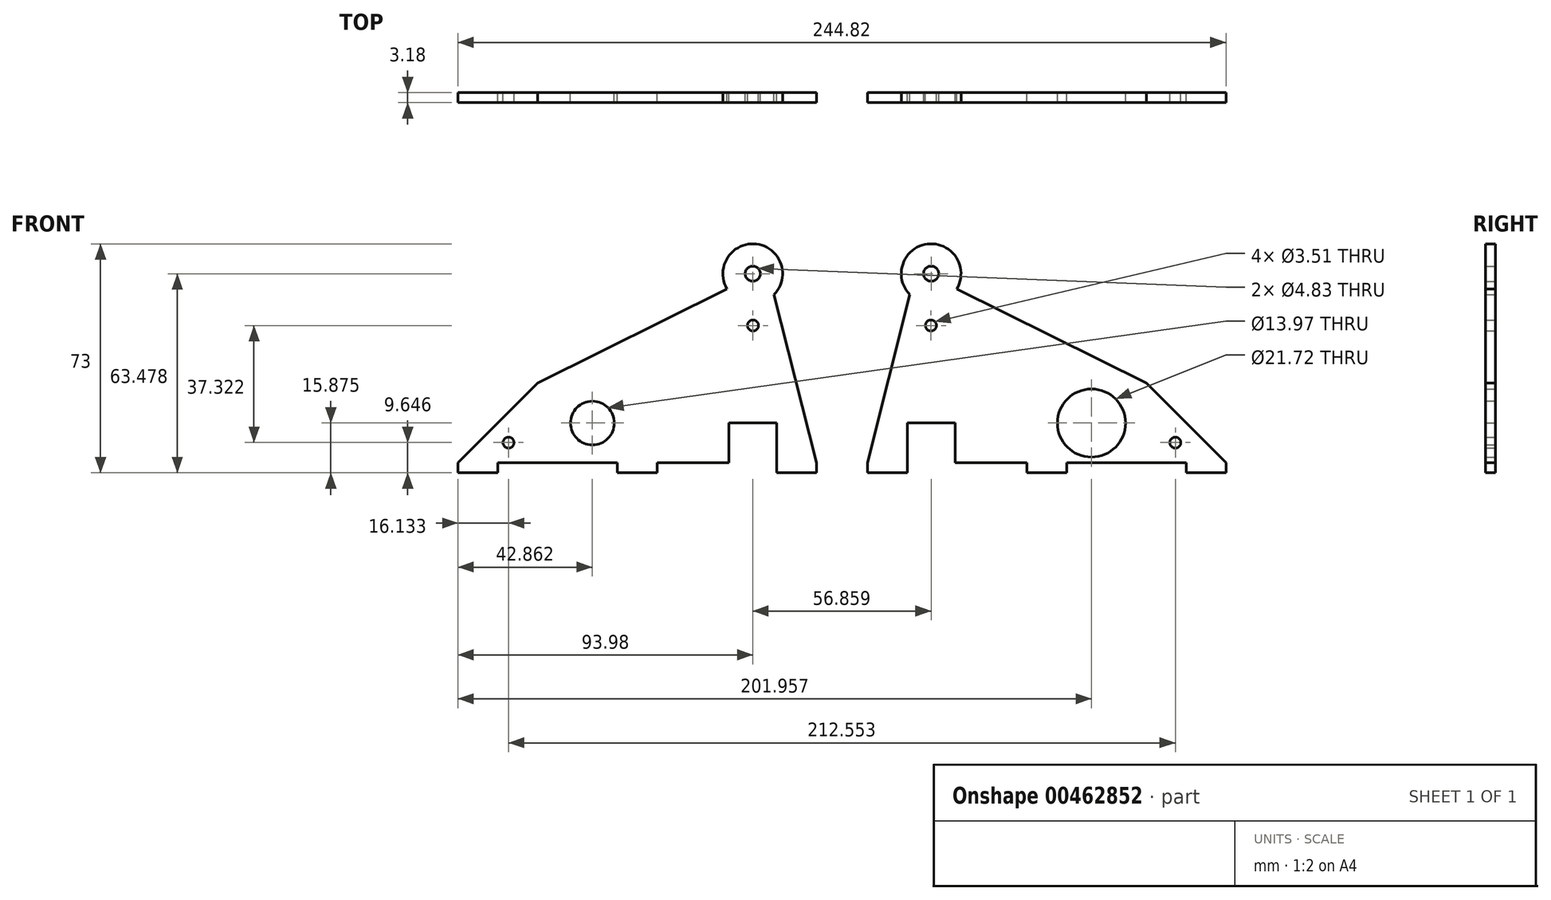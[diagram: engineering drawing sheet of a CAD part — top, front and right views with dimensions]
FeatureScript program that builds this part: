
annotation { "Feature Type Name" : "Feature", "Feature Type Description" : "" }
export const myFeature = defineFeature(function(context is Context, id is Id, definition is map)
    precondition{}
    {
        {
            var Q0;
            Q0=qCreatedBy(makeId("Front.planeOp"),FACE);
            var sketch = newSketch(context, id + "F0", { "sketchPlane" : qUnion([Q0])});
            skPoint(sketch, "E0.middle", {"position": v(0, 0) * mm});
            skLineSegment(sketch, "E1.bottom", {"start": v(-50.8, -34.93) * mm, "end": v(-12.7, -34.93) * mm});
            skLineSegment(sketch, "E1.left", {"start": v(-63.5, -34.92) * mm, "end": v(-63.5, -38.1) * mm});
            skLineSegment(sketch, "E2", {"start": v(-12.7, -34.93) * mm, "end": v(-12.7, -38.1) * mm});
            skLineSegment(sketch, "E3", {"start": v(0, -34.93) * mm, "end": v(0, -38.1) * mm});
            skLineSegment(sketch, "E4", {"start": v(50.8, -34.93) * mm, "end": v(50.8, -38.1) * mm});
            skLineSegment(sketch, "E5", {"start": v(38.1, -34.93) * mm, "end": v(38.1, -38.1) * mm});
            skLineSegment(sketch, "E6.trimOffspring", {"start": v(-12.7, -38.1) * mm, "end": v(0, -38.1) * mm});
            skLineSegment(sketch, "E7.trimOffspring", {"start": v(38.1, -38.1) * mm, "end": v(50.8, -38.1) * mm});
            skLineSegment(sketch, "E8", {"start": v(-38.1, -34.93) * mm, "end": v(-38.1, -9.53) * mm});
            skLineSegment(sketch, "E9", {"start": v(-38.1, -9.53) * mm, "end": v(-3.17, -9.53) * mm});
            skLineSegment(sketch, "E10", {"start": v(-3.17, -9.53) * mm, "end": v(-3.17, -34.92) * mm});
            skLineSegment(sketch, "E11", {"start": v(-38.1, -22.23) * mm, "end": v(-20.64, -22.23) * mm});
            skCircle(sketch, "E12", {"center": v(-20.64, -22.23) * mm, "radius": 6.99 * mm});
            skLineSegment(sketch, "E13", {"start": v(38.1, -34.93) * mm, "end": v(38.1, -22.23) * mm});
            skLineSegment(sketch, "E14", {"start": v(38.1, -22.22) * mm, "end": v(22.86, -22.23) * mm});
            skLineSegment(sketch, "E15", {"start": v(22.86, -22.23) * mm, "end": v(22.86, -34.93) * mm});
            skCircle(sketch, "E16", {"center": v(30.48, 25.38) * mm, "radius": 2.41 * mm});
            skCircle(sketch, "E17", {"center": v(30.48, 25.38) * mm, "radius": 9.53 * mm});
            skLineSegment(sketch, "E18", {"start": v(-50.8, -38.1) * mm, "end": v(-50.8, -34.92) * mm});
            skLineSegment(sketch, "E19", {"start": v(-50.8, -38.1) * mm, "end": v(-63.5, -38.1) * mm});
            skLineSegment(sketch, "E20", {"start": v(-63.5, -34.93) * mm, "end": v(-38.1, -9.53) * mm});
            skLineSegment(sketch, "E21", {"start": v(-38.1, -9.53) * mm, "end": v(22.28, 20.54) * mm});
            skLineSegment(sketch, "E22", {"start": v(37.24, 18.66) * mm, "end": v(50.8, -34.93) * mm});
            skCircle(sketch, "E23", {"center": v(30.55, 8.87) * mm, "radius": 1.75 * mm});
            skCircle(sketch, "E24", {"center": v(-47.37, -28.45) * mm, "radius": 1.75 * mm});
            skLineSegment(sketch, "E25.MirrorCS", {"start": v(181.32, -34.92) * mm, "end": v(181.32, -38.1) * mm});
            skLineSegment(sketch, "E26.MirrorCS", {"start": v(67.02, -34.93) * mm, "end": v(67.02, -38.1) * mm});
            skLineSegment(sketch, "E27.MirrorCS", {"start": v(168.62, -38.1) * mm, "end": v(168.62, -34.92) * mm});
            skLineSegment(sketch, "E28.MirrorCS", {"start": v(79.72, -34.93) * mm, "end": v(79.72, -38.1) * mm});
            skCircle(sketch, "E29.MirrorC", {"center": v(87.34, 25.38) * mm, "radius": 2.41 * mm});
            skCircle(sketch, "E30.MirrorC", {"center": v(165.19, -28.45) * mm, "radius": 1.75 * mm});
            skLineSegment(sketch, "E31.MirrorCS", {"start": v(79.72, -34.93) * mm, "end": v(79.72, -22.23) * mm});
            skLineSegment(sketch, "E32.MirrorCS", {"start": v(130.52, -34.93) * mm, "end": v(130.52, -38.1) * mm});
            skCircle(sketch, "E33.MirrorC", {"center": v(87.27, 8.87) * mm, "radius": 1.75 * mm});
            skLineSegment(sketch, "E34.MirrorCS", {"start": v(117.82, -34.93) * mm, "end": v(117.82, -38.1) * mm});
            skLineSegment(sketch, "E35.MirrorCS", {"start": v(79.72, -22.22) * mm, "end": v(94.96, -22.23) * mm});
            skLineSegment(sketch, "E36.MirrorCS", {"start": v(168.62, -34.93) * mm, "end": v(130.52, -34.93) * mm});
            skLineSegment(sketch, "E37.MirrorCS", {"start": v(121, -9.53) * mm, "end": v(121, -34.92) * mm});
            skLineSegment(sketch, "E38.MirrorCS", {"start": v(181.32, -34.93) * mm, "end": v(155.92, -9.53) * mm});
            skLineSegment(sketch, "E39.MirrorCS", {"start": v(155.92, -34.93) * mm, "end": v(155.92, -9.53) * mm});
            skLineSegment(sketch, "E40.MirrorCS", {"start": v(155.92, -22.23) * mm, "end": v(138.46, -22.23) * mm});
            skCircle(sketch, "E41.MirrorC", {"center": v(87.34, 25.38) * mm, "radius": 9.53 * mm});
            skLineSegment(sketch, "E42.MirrorCS", {"start": v(94.96, -22.23) * mm, "end": v(94.96, -34.93) * mm});
            skLineSegment(sketch, "E43.MirrorCS", {"start": v(80.58, 18.66) * mm, "end": v(67.02, -34.93) * mm});
            skPoint(sketch, "E44.MirrorP", {"position": v(117.82, 0) * mm});
            skLineSegment(sketch, "E45.MirrorCS", {"start": v(130.52, -38.1) * mm, "end": v(117.82, -38.1) * mm});
            skLineSegment(sketch, "E46.MirrorCS", {"start": v(155.92, -9.53) * mm, "end": v(121, -9.53) * mm});
            skLineSegment(sketch, "E47.MirrorCS", {"start": v(155.92, -9.53) * mm, "end": v(95.54, 20.54) * mm});
            skLineSegment(sketch, "E48.MirrorCS", {"start": v(168.62, -38.1) * mm, "end": v(181.32, -38.1) * mm});
            skLineSegment(sketch, "E49.MirrorCS", {"start": v(79.72, -38.1) * mm, "end": v(67.02, -38.1) * mm});
            skCircle(sketch, "E50.MirrorC", {"center": v(138.46, -22.23) * mm, "radius": 10.86 * mm});
            skLineSegment(sketch, "E51.trimOffspring", {"start": v(94.96, -34.93) * mm, "end": v(117.82, -34.93) * mm});
            skLineSegment(sketch, "E52.trimOffspring", {"start": v(22.86, -34.93) * mm, "end": v(0, -34.93) * mm});
            skLineSegment(sketch, "E53.trimOffspring", {"start": v(-12.7, -34.93) * mm, "end": v(-50.8, -34.92) * mm});
            skLineSegment(sketch, "E54.trimOffspring", {"start": v(0, -34.93) * mm, "end": v(22.86, -34.93) * mm});
            skLineSegment(sketch, "E55.trimOffspring", {"start": v(130.52, -34.93) * mm, "end": v(168.62, -34.92) * mm});
            skLineSegment(sketch, "E56.trimOffspring", {"start": v(117.82, -34.93) * mm, "end": v(94.96, -34.93) * mm});
            skSolve(sketch);
        }
        {
            var Q0;
            Q0 = qSketchRegion(id + "F0", true);
            extrude(context, id + "F1", {"entities" : qUnion([Q0]), "depth" : 3.17 * mm});
        }
    });
